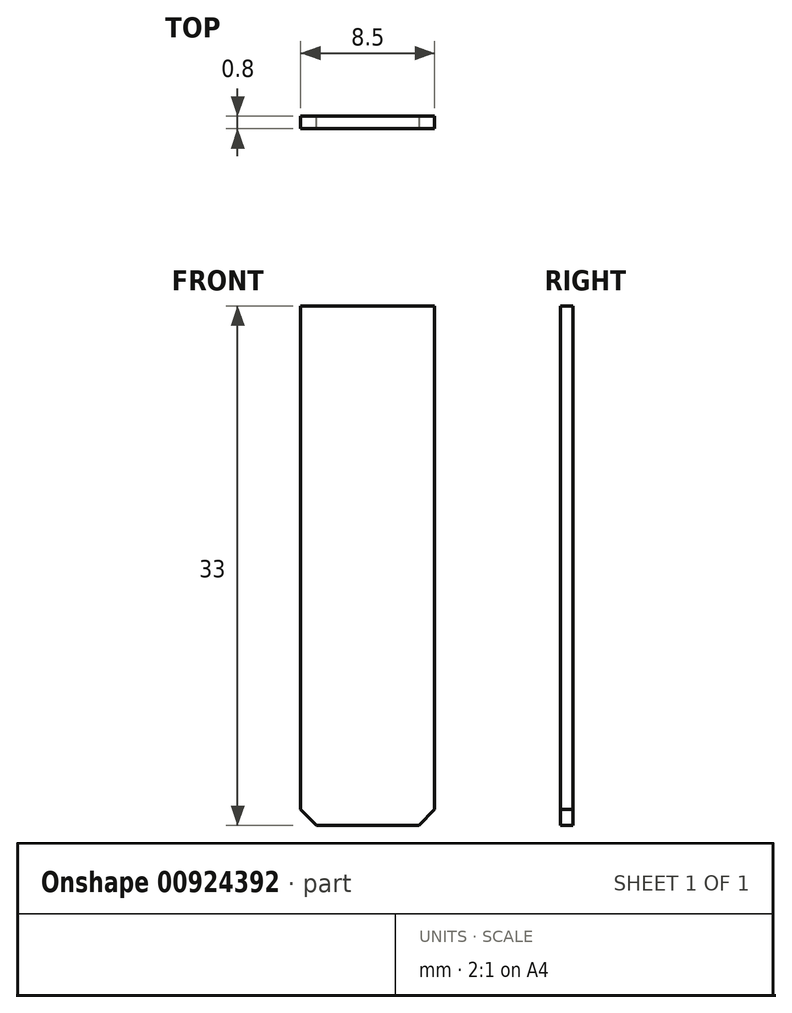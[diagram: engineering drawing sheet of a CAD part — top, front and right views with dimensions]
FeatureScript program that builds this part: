
annotation { "Feature Type Name" : "Feature", "Feature Type Description" : "" }
export const myFeature = defineFeature(function(context is Context, id is Id, definition is map)
    precondition{}
    {
        {
            var Q0;
            Q0=qCreatedBy(makeId("Front.planeOp"),FACE);
            var sketch = newSketch(context, id + "F0", { "sketchPlane" : qUnion([Q0])});
            skLineSegment(sketch, "E0.bottom", {"start": v(0, 0) * mm, "end": v(8.5, 0) * mm});
            skLineSegment(sketch, "E0.top", {"start": v(0, 33) * mm, "end": v(8.5, 33) * mm});
            skLineSegment(sketch, "E0.left", {"start": v(0, 0) * mm, "end": v(0, 33) * mm});
            skLineSegment(sketch, "E0.right", {"start": v(8.5, 0) * mm, "end": v(8.5, 33) * mm});
            skSolve(sketch);
        }
        {
            var Q0;
            Q0=makeQuery(id+"F0.imprint","IMPRINT",FACE,{"disambiguationData":[TD([[makeQuery(id+"F0.imprint","IMPRINT",EDGE,{"derivedFrom":sQuery(id+"F0.wireOp",EDGE,"E0.bottom")}),1.0]])]});
            extrude(context, id + "F1", {"entities" : qUnion([Q0]), "depth" : .8 * mm, "offsetDistance" : 25 * mm});
        }
        {
            var Q0;
            Q0=makeQuery(id+"F1.opExtrude","SWEPT_EDGE",EDGE,{"disambiguationData":[OSD([sQuery(id+"F0.wireOp",EDGE,"E0.bottom"),sQuery(id+"F0.wireOp",EDGE,"E0.right")])]});
            var Q1;
            Q1=makeQuery(id+"F1.opExtrude","SWEPT_EDGE",EDGE,{"disambiguationData":[OSD([sQuery(id+"F0.wireOp",EDGE,"E0.bottom"),sQuery(id+"F0.wireOp",EDGE,"E0.left")])]});
            chamfer(context, id + "F2", {"entities" : qUnion([Q0, Q1]), "width" : 1 * mm, "tangentPropagation" : true});
        }
    });
